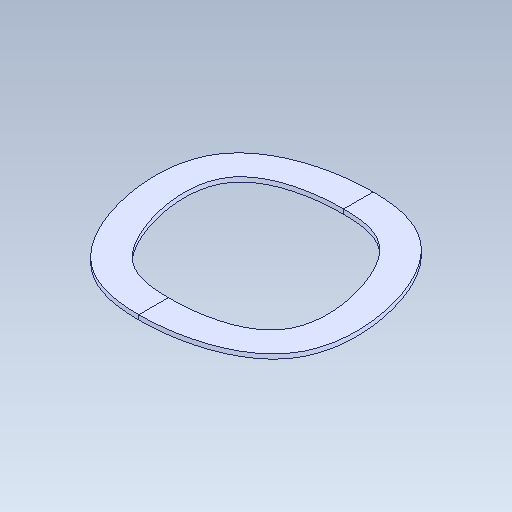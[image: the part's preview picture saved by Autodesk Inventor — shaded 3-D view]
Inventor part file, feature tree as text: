
AUTODESK INVENTOR PART (.ipt)
format: ipt  version: 2020 (Build 240168000, 168)  size: 114,688 bytes
history: native  units: in
note: dims shown in document units (in); Inventor stores cm internally (conversion verified against a paired STEP export)
features: loft x1
ambient origin geometry x8: Origin, YZ Plane, XZ Plane, XY Plane, X Axis, Y Axis, Z Axis, Center Point
bodies: Solid1 (feature_tree)
feature tree (1):
  loft  "Loft1"
